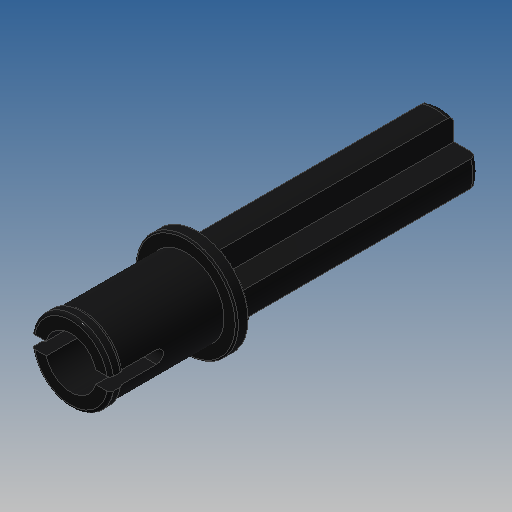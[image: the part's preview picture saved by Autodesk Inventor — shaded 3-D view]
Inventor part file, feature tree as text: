
AUTODESK INVENTOR PART (.ipt)
format: ipt  version: 2022.2 (Build 262287000, 287)  size: 252,928 bytes
history: native  units: mm (DEFAULTED — no unit token found)
features: sketch x3, fillet x2, extrude x2, revolve x1
ambient origin geometry x8: Origin, YZ Plane, XZ Plane, XY Plane, X Axis, Y Axis, Z Axis, Center Point
bodies: Solid2 (feature_tree)
feature tree (8):
  revolve  "Revolution1"  [1 undecoded]
  fillet  "Fillet1"  Radius=0.75mm
  extrude  "Extrusion2"  Depth=6.4mm
  extrude  "Extrusion3"  Depth=0.4mm
  fillet  "Fillet2"  [1 undecoded]
  sketch  "Sketch1"  dims[d1=4.8mm d2=5.0mm d4=0.75mm]
  sketch  "Sketch2"  dims[d7=0.8mm d8=6.4mm]
  sketch  "Sketch3"  dims[d9=0.8mm d19=8.0mm d20=90.0deg d25=10.0mm d26=0.0mm d27=0.2mm d28=0.1mm d30=0.0mm d34=3.4mm d35=4.8mm d36=1.6mm d37=15.2mm d38=0.0mm d39=0.4mm d40=3.2mm d41=0.8mm d42=0.0mm d43=0.0mm d44=0.0mm d46=8.0mm]
note: 2 required parameter values undecoded (feature->parameter linkage not recoverable at this tier; creation-order binding heuristic only, values carry confidence <= 0.55)